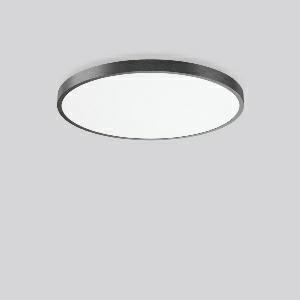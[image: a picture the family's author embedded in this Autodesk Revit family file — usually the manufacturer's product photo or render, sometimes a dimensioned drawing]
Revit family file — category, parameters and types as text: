
# Revit family: triona_round_a_312387_0031_2_730_f817
name_source: partatom
category: Lighting Fixtures
units: mm (PartAtom-declared; Revit-internal decimal feet)

## family parameters
Cut with Voids When Loaded = No
Host = Face
Light Source = No
Part Type = Normal
Room Calculation Point = No
Round Connector Dimension = Use Diameter
Shared = No

## types (1)
- TuneableWhite 846 (1 x LED Modul 846, 4800 lm, 4600)
    Apparent Load = 49 VA
    CIE Flux Codes = 50 80 96 100 100
    Color Rendering = 80
    Color Temperature = 4600
    Default Elevation = 1800 mm
    Description = Series: TRIONA round
Decorative round LED surface-mounted luminaire. Flat, seamless frame: aluminium extrusion profile, powder coated. Cover made of sheet steel, powder-coated. Light emission through a diffuser: plastic, opal. Lightguide and diffuser made of non-yellowing plastic (PMMA). Lateral light emission (RZB SIDELITE technology) for above-average homogeneous light distribution. Tunable white versions, dynamically adjustable from 2700 K to 6500 K. Suitable for Ceiling mounting, Wall (surface). Tool-free mounting via bayonet connection. Electronic ballast included. Very easy installation thanks to Plug+Play connection. With Casambi smart+free Bluetooth control for wireless network and operation using Android / iOS devices, free app available for download. Ideal for use as part of the Human Centric Lighting concept in connection with RZB light management systems. 
Colour: anthracite metallic (DB703)
Diameter: 845 mm
Height: 88 mm
Lamp: LED
Socket: without socket
Colour temperature: 2700K - 6500K
Colour rendering index (CRI): 80
System power: 49 W
Rated luminous flux: 4800 lm
Luminous efficiency: 98 lm/W
System power 2: 51 W
Rated luminous flux 2: 4550 lm
Luminous efficiency 2: 89 lm/W
System power 3: 51 W
Rated luminous flux 3: 4650 lm
Luminous efficiency 3: 91 lm/W
Control gear: Dimmable Bluetooth converter
Protection class: I
Type of protection: IP 20
    Height = 88 mm
    Lamp = 1 x LED Modul 846
    Lamp Light Flux = 4800 lm
    Lamp count = 1
    Length = 845 mm
    Lifetime = 50000 h
    Luminous efficacy = 98 lm/W
    Manufacturer = RZB
    ModVariant = No
    Model = 312387.0031.2.730
    Mounting Place = Ceiling
    Mounting Type = Surface mounted
    Number of Poles = 1
    OnlyDefault = Yes
    Power Factor = 1
    Product Name = TRIONA round A
    Product group = Surface mounted modular luminaires
    ProductGroupID = 306
    Protection Class = Protection class I
    Protection Degree = IP 20
    RLX_Detail_Level = 1
    RLX_Emergency_Light_Flux = 0 lm
    RLX_Emergency_Type = 0
    RLX_Emergency_Type_DB = No
    RlxData = <blob elided: 37165 chars, md5=3e791b97>
    Socket = socket
    Standby Power = 0 W
    System Light Flux = 4800 lm
    System Power = 49 W
    Type Comments = TuneableWhite 846
    Type Image = 312388.0031.jpg
    URL = http://relux.com
    VarID = tuneablewhite_846
    Voltage = 230 V
    Voltage Range = 220-240 V
    Weight = 0.00 kg
    Width = 0 mm  [stored 0 ft]

note: [stored X ft] marks values corroborated as IEEE doubles in the binary element streams (Revit-internal decimal feet)

## geometry (parser evidence)
native form markers: Blend x4, Sweep x9
no freeform markers — native parametric forms only
